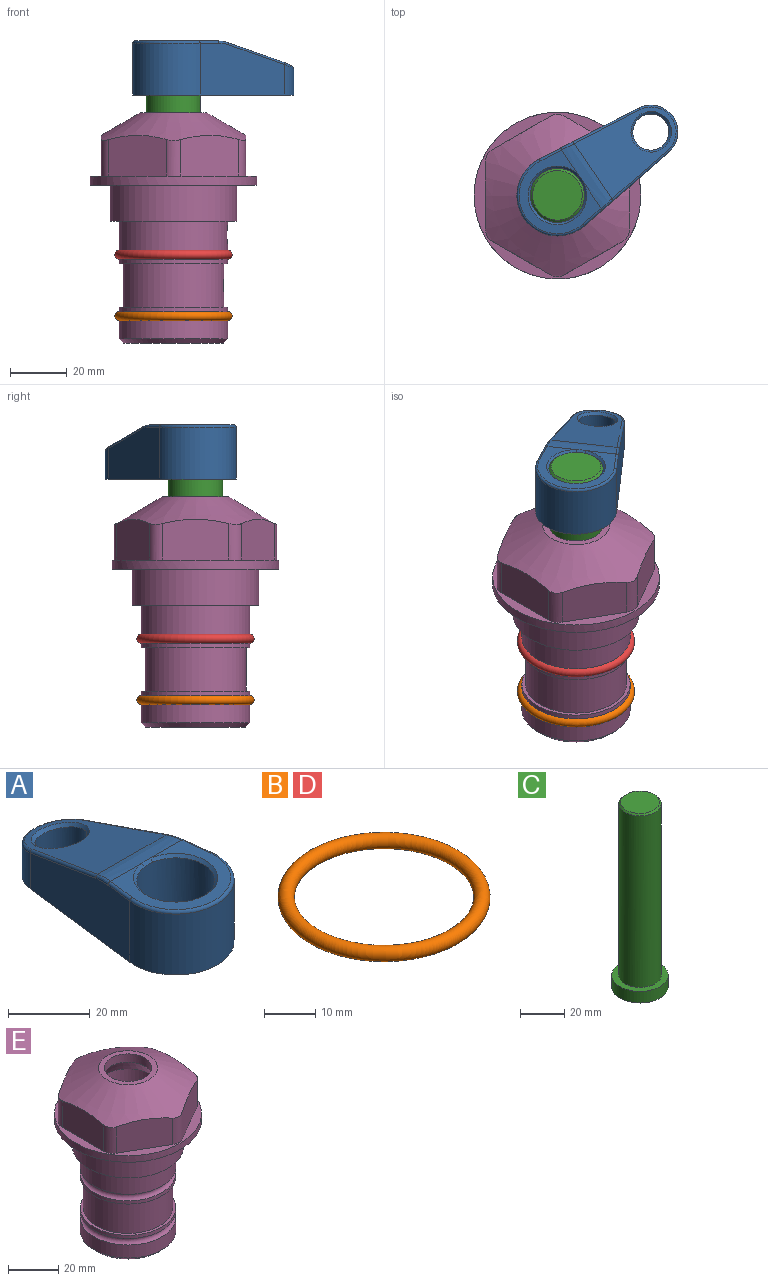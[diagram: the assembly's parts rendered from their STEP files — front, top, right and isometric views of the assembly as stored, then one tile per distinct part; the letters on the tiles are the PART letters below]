
ASSEMBLY  parts=5 mates=4
PART A: 31 faces, bbox 31.7x65.5x19.8 mm
  f0: plane 39.12x18.26mm, normal (0.99,0.12,0), area 612.2mm2, adj f1,f4,f7,f11,f13,f15
  f1: cylinder r=9.53mm len=18.91mm, axis (0,0,-1), area 296.1mm2, adj f0,f2,f7,f17
  f2: plane 39.12x18.26mm, normal (-0.99,0.12,0), area 612.2mm2, adj f1,f4,f7,f12,f14,f16
  f3: cylinder r=6.35mm len=12.7mm, axis (0,0,-1), area 362.4mm2, adj f7,f18
  f4: cylinder r=14.29mm len=28.58mm, axis (0,0,-1), area 882.2mm2, adj f0,f2,f7,f10
  f5: cylinder r=9.53mm len=19.05mm, axis (0,0,-1), area 1092.6mm2, adj f7,f19,f20
  f6: plane 26.99x23.69mm, normal (0,0,1), area 216.2mm2, adj f9,f10,f11,f12,f19
  f7: plane 63.5x28.58mm, normal (0,0,-1), area 661.8mm2, adj f0,f1,f2,f3,f4,f5,f22,f23
  f8: plane 33.52x23.6mm, normal (0,0.26,0.97), area 486mm2, adj f9,f15,f16,f17,f18
  f9: cylinder r=19.05mm len=24.72mm, axis (1,0,0), area 120.4mm2, adj f6,f8,f13,f14,f20
  f10: torus R=13.49mm, axis (0,0,1), area 59mm2, adj f4,f6,f11,f12
  f11: cylinder r=0.79mm len=8.67mm, axis (0.12,-0.99,0), area 10.8mm2, adj f0,f6,f10,f13
  f12: cylinder r=0.79mm len=8.67mm, axis (0.12,0.99,0), area 10.8mm2, adj f2,f6,f10,f14
  f13: bspline ~4.95x1.42mm, area 6.1mm2, adj f0,f9,f11,f15
  f14: bspline ~4.95x1.42mm, area 6.1mm2, adj f2,f9,f12,f16
  f15: cylinder r=0.79mm len=25.95mm, axis (0.12,-0.96,0.26), area 32.9mm2, adj f0,f8,f13,f17
  f16: cylinder r=0.79mm len=25.95mm, axis (0.12,0.96,-0.26), area 32.9mm2, adj f2,f8,f14,f17
  f17: bspline ~18.91x8.38mm, area 30mm2, adj f1,f8,f15,f16
  f18: bspline ~14.29x14.29mm, area 48.3mm2, adj f3,f8
  f19: cone r=9.53mm half-angle=45deg, axis (0,0,1), area 66.5mm2, adj f5,f6,f20
  f20: bspline ~3.22x0.96mm, area 3.5mm2, adj f5,f9,f19
  f21: plane 2.75x2.72mm, normal (0,0,-1), area 2.9mm2, adj f23,f25,f28
  f22: plane 23.05x15.88mm, normal (-0.99,-0.12,0), area 323.6mm2, adj f7,f25,f26,f27,f28,f29
  f23: plane 23.05x15.88mm, normal (0.99,-0.12,0), area 323.6mm2, adj f7,f21,f25,f27,f28,f30
  f24: cylinder r=9.53mm len=10.69mm, axis (0,0,-1), area 114.7mm2, adj f7,f27,f29,f30
  f25: cylinder r=12.7mm len=20.59mm, axis (0,0,-1), area 381.1mm2, adj f7,f21,f22,f23,f26,f28
  f26: plane 2.75x2.72mm, normal (0,0,-1), area 2.9mm2, adj f22,f25,f28
  f27: plane 19.72x18.37mm, normal (0,-0.26,-0.97), area 291.8mm2, adj f22,f23,f24,f28,f29,f30
  f28: cylinder r=15.88mm len=19.92mm, axis (1,0,0), area 54.8mm2, adj f21,f22,f23,f25,f26,f27
  f29: cylinder r=1.59mm len=11mm, axis (0,0,-1), area 34.7mm2, adj f7,f22,f24,f27
  f30: cylinder r=1.59mm len=11mm, axis (0,0,-1), area 34.7mm2, adj f7,f23,f24,f27
PART B: 1 faces, bbox 44.7x44.7x3.2 mm
  f0: torus R=19.05mm, axis (0,0,1), area 1193.9mm2
PART C: 6 faces, bbox 25.4x25.4x101.6 mm
  f0: plane 17.46x17.46mm, normal (0,0,1), area 239.5mm2, adj f5
  f1: plane 25.4x25.4mm, normal (0,0,-1), area 506.7mm2, adj f2
  f2: cylinder r=12.7mm len=25.4mm, axis (0,0,1), area 506.7mm2, adj f1,f3
  f3: plane 25.4x25.4mm, normal (0,0,1), area 221.7mm2, adj f2,f4
  f4: cylinder r=9.53mm len=94.46mm, axis (0,0,1), area 5653mm2, adj f3,f5
  f5: cone r=8.73mm half-angle=45deg, axis (0,0,-1), area 64.4mm2, adj f0,f4
PART D: same geometry as B
PART E: 36 faces, bbox 58.7x58.7x81 mm
  f0: cylinder r=17.78mm len=35.56mm, axis (0,0,1), area 1670.8mm2, adj f23,f24,f31
  f1: cylinder r=19.05mm len=38.1mm, axis (0,0,1), area 1191.9mm2, adj f26,f27,f30
  f2: plane 58.66x58.66mm, normal (0,0,-1), area 1150.6mm2, adj f3,f28
  f3: cylinder r=29.33mm len=58.66mm, axis (0,0,-1), area 585.1mm2, adj f2,f4
  f4: plane 58.66x58.66mm, normal (0,0,1), area 475.9mm2, adj f3,f5,f6,f7,f8,f9,f10,f11
  f5: plane 20.32x14.34mm, normal (-0.5,0.87,0), area 324.4mm2, adj f4,f15,f16,f17
  f6: plane 20.32x14.34mm, normal (0.5,0.87,0), area 324.4mm2, adj f4,f14,f15,f17
  f7: plane 23.48x14.34mm, normal (1,0,0), area 324.4mm2, adj f4,f13,f14,f17
  f8: plane 20.32x14.34mm, normal (0.5,-0.87,0), area 324.4mm2, adj f4,f12,f13,f17
  f9: plane 20.32x14.34mm, normal (-0.5,-0.87,0), area 324.4mm2, adj f4,f11,f12,f17
  f10: plane 23.48x14.34mm, normal (-1,0,0), area 324.4mm2, adj f4,f11,f16,f17
  f11: cylinder r=5.08mm len=12.85mm, axis (0,0,-1), area 67.2mm2, adj f4,f9,f10,f17
  f12: cylinder r=5.08mm len=12.85mm, axis (0,0,-1), area 67.2mm2, adj f4,f8,f9,f17
  f13: cylinder r=5.08mm len=12.85mm, axis (0,0,-1), area 67.2mm2, adj f4,f7,f8,f17
  f14: cylinder r=5.08mm len=12.85mm, axis (0,0,-1), area 67.2mm2, adj f4,f6,f7,f17
  f15: cylinder r=5.08mm len=12.85mm, axis (0,0,-1), area 67.2mm2, adj f4,f5,f6,f17
  f16: cylinder r=5.08mm len=12.85mm, axis (0,0,-1), area 67.2mm2, adj f4,f5,f10,f17
  f17: cone r=11.73mm half-angle=60deg, axis (0,0,-1), area 2071.8mm2, adj f5,f6,f7,f8,f9,f10,f11,f12
  f18: plane 23.46x23.46mm, normal (0,0,1), area 147.4mm2, adj f17,f35
  f19: plane 34.93x34.93mm, normal (0,0,-1), area 958mm2, adj f29
  f20: cylinder r=19.05mm len=38.1mm, axis (0,0,1), area 760.1mm2, adj f21,f29
  f21: torus R=19.05mm, axis (0,0,1), area 565.3mm2, adj f20,f22
  f22: cylinder r=19.05mm len=38.1mm, axis (0,0,1), area 190mm2, adj f21,f23
  f23: plane 38.1x38.1mm, normal (0,0,1), area 146.9mm2, adj f0,f22
  f24: plane 38.1x38.1mm, normal (0,0,-1), area 146.9mm2, adj f0,f25
  f25: cylinder r=19.05mm len=38.1mm, axis (0,0,1), area 190mm2, adj f24,f26
  f26: torus R=19.05mm, axis (0,0,1), area 565.3mm2, adj f1,f25
  f27: plane 44.45x44.45mm, normal (0,0,-1), area 411.7mm2, adj f1,f28
  f28: cylinder r=22.23mm len=44.45mm, axis (0,0,1), area 1773.5mm2, adj f2,f27
  f29: cone r=19.05mm half-angle=45deg, axis (0,0,1), area 257.5mm2, adj f19,f20
  f30: cylinder r=3.17mm len=6.75mm, axis (-1,0,0), area 128mm2, adj f1,f33
  f31: cylinder r=3.17mm len=6.35mm, axis (-1,0,0), area 102.5mm2, adj f0,f33
  f32: plane 25.4x25.4mm, normal (0,0,1), area 506.7mm2, adj f33
  f33: cylinder r=12.7mm len=66.42mm, axis (0,0,-1), area 5236.2mm2, adj f30,f31,f32,f34
  f34: cone r=9.53mm half-angle=30deg, axis (0,0,-1), area 443.4mm2, adj f33,f35
  f35: cylinder r=9.53mm len=19.05mm, axis (0,0,-1), area 240.9mm2, adj f18,f34
PLACE A rot(axis=(0,0,-1),55.9deg) t=(0,0,-12.76)mm
PLACE B t=(0,0,-21.59)mm
PLACE C rot(axis=(0,0,-1),55.9deg) t=(0,0,-12.76)mm
PLACE D at identity
PLACE E at identity fixed
MATE cylindrical C.f2 <-> E.f0  axis (0,0,-1) through (0,0,-50.86)mm
MATE fastened C.f2 <-> A.f4  axis (0,0,1) through (0,0,50.74)mm
MATE fastened D.f0 <-> E.f0  axis (0,0,1) through (0,0,-24.51)mm
MATE fastened B.f0 <-> E.f0  axis (0,0,1) through (0,0,-46.1)mm
